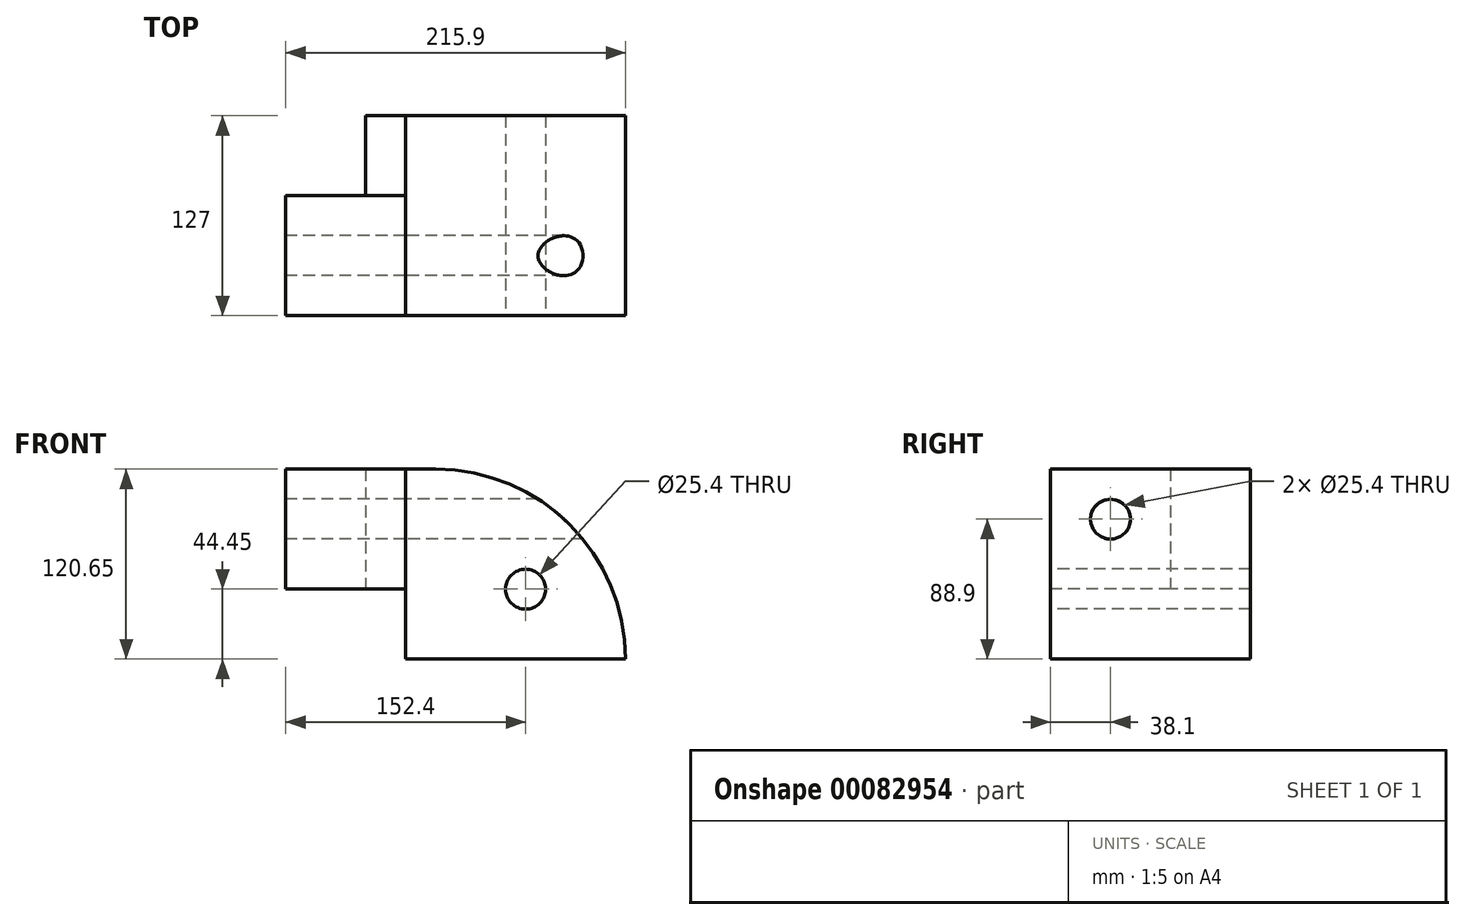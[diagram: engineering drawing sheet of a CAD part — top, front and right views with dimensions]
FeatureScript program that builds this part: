
annotation { "Feature Type Name" : "Feature", "Feature Type Description" : "" }
export const myFeature = defineFeature(function(context is Context, id is Id, definition is map)
    precondition{}
    {
        {
            var Q0;
            Q0=qCreatedBy(makeId("Front.planeOp"),FACE);
            var sketch = newSketch(context, id + "F0", { "sketchPlane" : qUnion([Q0])});
            skArc(sketch, "E0", {"start": v(120.65, 0) * mm, "mid": v(85.31, 85.31) * mm, "end": v(0, 120.65) * mm});
            skLineSegment(sketch, "E1", {"start": v(120.65, 0) * mm, "end": v(0, 0) * mm});
            skLineSegment(sketch, "E2.left", {"start": v(0, 120.65) * mm, "end": v(0, 44.45) * mm});
            skLineSegment(sketch, "E3", {"start": v(0, 44.45) * mm, "end": v(0, 0) * mm});
            skPoint(sketch, "E4", {"position": v(57.15, 44.45) * mm});
            skLineSegment(sketch, "E5.bottom", {"start": v(0, 120.65) * mm, "end": v(-19.05, 120.65) * mm});
            skLineSegment(sketch, "E5.top", {"start": v(0, 0) * mm, "end": v(-19.05, 0) * mm});
            skLineSegment(sketch, "E5.left", {"start": v(0, 120.65) * mm, "end": v(0, 0) * mm});
            skLineSegment(sketch, "E5.right", {"start": v(-19.05, 120.65) * mm, "end": v(-19.05, 0) * mm});
            skLineSegment(sketch, "E6.bottom", {"start": v(-19.05, 120.65) * mm, "end": v(-95.25, 120.65) * mm});
            skLineSegment(sketch, "E6.top", {"start": v(-19.05, 44.45) * mm, "end": v(-95.25, 44.45) * mm});
            skLineSegment(sketch, "E6.left", {"start": v(-19.05, 120.65) * mm, "end": v(-19.05, 44.45) * mm});
            skLineSegment(sketch, "E6.right", {"start": v(-95.25, 120.65) * mm, "end": v(-95.25, 44.45) * mm});
            skSolve(sketch);
        }
        {
            var Q0;
            Q0=makeQuery(id+"F0.imprint","IMPRINT",FACE,{"disambiguationData":[TD([[makeQuery(id+"F0.imprint","IMPRINT",EDGE,{"derivedFrom":sQuery(id+"F0.wireOp",EDGE,"E0")}),1.0]])]});
            extrude(context, id + "F1", {"entities" : qUnion([Q0]), "oppositeDirection" : true, "depth" : 127 * mm});
        }
        {
            var Q0;
            Q0=makeQuery(id+"F0.imprint","IMPRINT",FACE,{"disambiguationData":[TD([[makeQuery(id+"F0.imprint","IMPRINT",EDGE,{"derivedFrom":sQuery(id+"F0.wireOp",EDGE,"E2.bottom")}),1.0]])]});
            var Q1;
            {var subQ3=sQuery(id+"F0.wireOp",EDGE,"E5.bottom");Q1=makeQuery(id+"F0.imprint","IMPRINT",FACE,{"disambiguationData":[TD([[makeQuery(id+"F0.imprint","IMPRINT",EDGE,{"derivedFrom":subQ3}),1.0]])]});}
            extrude(context, id + "F2", {"entities" : qUnion([Q0, Q1]), "operationType" : NewBodyOperationType.ADD, "oppositeDirection" : true, "depth" : 127 * mm});
        }
        {
            var Q0;
            Q0=sQuery(id+"F0.wireOp",VERTEX,"E4");
            var Q1;
            Q1=makeQuery(id+"F1.opExtrude","SWEPT_BODY",BODY,{"disambiguationData":[OSD([sQuery(id+"F0.wireOp",EDGE,"E0"),sQuery(id+"F0.wireOp",EDGE,"E1"),sQuery(id+"F0.wireOp",EDGE,"E2.left"),sQuery(id+"F0.wireOp",EDGE,"E3")])]});
            hole(context, id + "F3", {"style" : HoleStyle.SIMPLE, "endStyle" : HoleEndStyle.THROUGH, "holeDiameter" : 25.4 * mm, "locations" : qUnion([Q0]), "scope" : qUnion([Q1]), "isTappedThrough" : true});
        }
        {
            var Q0;
            Q0=makeQuery(id+"F0.imprint","IMPRINT",FACE,{"disambiguationData":[TD([[makeQuery(id+"F0.imprint","IMPRINT",EDGE,{"derivedFrom":sQuery(id+"F0.wireOp",EDGE,"E6.bottom")}),1.0]])]});
            extrude(context, id + "F4", {"entities" : qUnion([Q0]), "oppositeDirection" : true, "depth" : 76.2 * mm});
        }
        {
            var Q0;
            Q0=makeQuery(id+"F4.opExtrude","SWEPT_FACE",FACE,{"disambiguationData":[OSD([sQuery(id+"F0.wireOp",EDGE,"E6.right")])]});
            var sketch = newSketch(context, id + "F5", { "sketchPlane" : qUnion([Q0])});
            skPoint(sketch, "E7", {"position": v(-38.1, 88.9) * mm});
            skSolve(sketch);
        }
        {
            var Q0;
            Q0=sQuery(id+"F5.wireOp",VERTEX,"E7");
            var Q1;
            Q1=makeQuery(id+"F4.opExtrude","SWEPT_BODY",BODY,{"disambiguationData":[OSD([sQuery(id+"F0.wireOp",EDGE,"E6.bottom"),sQuery(id+"F0.wireOp",EDGE,"E6.top"),sQuery(id+"F0.wireOp",EDGE,"E6.left"),sQuery(id+"F0.wireOp",EDGE,"E6.right")])]});
            hole(context, id + "F6", {"style" : HoleStyle.SIMPLE, "endStyle" : HoleEndStyle.THROUGH, "holeDiameter" : 25.4 * mm, "locations" : qUnion([Q0]), "scope" : qUnion([Q1]), "isTappedThrough" : true});
        }
        {
            var Q0;
            Q0=makeQuery(id+"F2.opExtrude","SWEPT_FACE",FACE,{"disambiguationData":[OSD([sQuery(id+"F0.wireOp",EDGE,"E5.right"),sQuery(id+"F0.wireOp",EDGE,"E6.left")])]});
            var sketch = newSketch(context, id + "F7", { "sketchPlane" : qUnion([Q0])});
            skPoint(sketch, "E8", {"position": v(-38.1, 88.9) * mm});
            skSolve(sketch);
        }
        {
            var Q0;
            Q0=sQuery(id+"F7.wireOp",VERTEX,"E8");
            var Q1;
            Q1=makeQuery(id+"F1.opExtrude","SWEPT_BODY",BODY,{"disambiguationData":[OSD([sQuery(id+"F0.wireOp",EDGE,"E0"),sQuery(id+"F0.wireOp",EDGE,"E1"),sQuery(id+"F0.wireOp",EDGE,"E5.left")])]});
            hole(context, id + "F8", {"style" : HoleStyle.SIMPLE, "endStyle" : HoleEndStyle.THROUGH, "holeDiameter" : 25.4 * mm, "locations" : qUnion([Q0]), "scope" : qUnion([Q1]), "isTappedThrough" : true});
        }
        {
            var Q0;
            Q0=makeQuery(id+"F2.opExtrude","SWEPT_FACE",FACE,{"disambiguationData":[OSD([sQuery(id+"F0.wireOp",EDGE,"E5.right"),sQuery(id+"F0.wireOp",EDGE,"E6.left")])]});
            var sketch = newSketch(context, id + "F9", { "sketchPlane" : qUnion([Q0])});
            skLineSegment(sketch, "E9.bottom", {"start": v(-127, 120.65) * mm, "end": v(-76.2, 120.65) * mm});
            skLineSegment(sketch, "E9.top", {"start": v(-127, 44.45) * mm, "end": v(-76.2, 44.45) * mm});
            skLineSegment(sketch, "E9.left", {"start": v(-127, 120.65) * mm, "end": v(-127, 44.45) * mm});
            skLineSegment(sketch, "E9.right", {"start": v(-76.2, 120.65) * mm, "end": v(-76.2, 44.45) * mm});
            skSolve(sketch);
        }
        {
            var Q0;
            Q0=makeQuery(id+"F9.imprint","IMPRINT",FACE,{"disambiguationData":[TD([[makeQuery(id+"F9.imprint","IMPRINT",EDGE,{"derivedFrom":sQuery(id+"F9.wireOp",EDGE,"E9.bottom")}),-1.0]])]});
            extrude(context, id + "F10", {"entities" : qUnion([Q0]), "depth" : 25.4 * mm});
        }
    });
